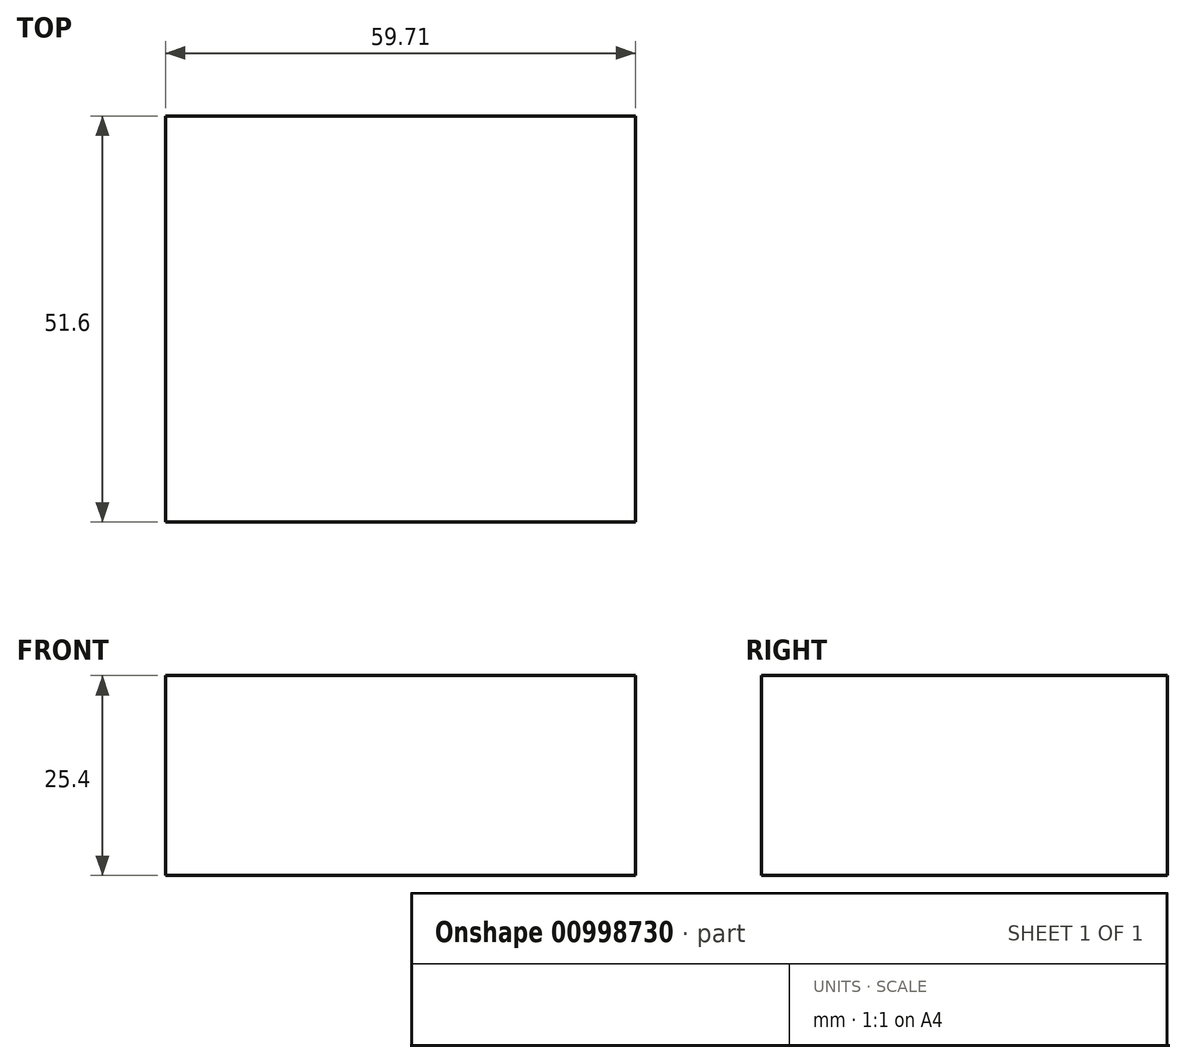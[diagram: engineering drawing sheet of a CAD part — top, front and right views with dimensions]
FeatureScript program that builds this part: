
annotation { "Feature Type Name" : "Feature", "Feature Type Description" : "" }
export const myFeature = defineFeature(function(context is Context, id is Id, definition is map)
    precondition{}
    {
        {
            var Q0;
            Q0=qCreatedBy(makeId("Top.planeOp"),FACE);
            var sketch = newSketch(context, id + "F0", { "sketchPlane" : qUnion([Q0])});
            skLineSegment(sketch, "E0.bottom", {"start": v(-91.76, -40.56) * mm, "end": v(-187.36, -40.56) * mm});
            skLineSegment(sketch, "E0.top", {"start": v(-91.76, 11.04) * mm, "end": v(-187.36, 11.04) * mm});
            skLineSegment(sketch, "E0.left", {"start": v(-91.76, -40.56) * mm, "end": v(-91.76, 11.04) * mm});
            skLineSegment(sketch, "E0.right", {"start": v(-187.36, -40.56) * mm, "end": v(-187.36, 11.04) * mm});
            skPoint(sketch, "E0.middle", {"position": v(-139.56, -14.76) * mm});
            skLineSegment(sketch, "E1.bottom", {"start": v(-121.22, 105.1) * mm, "end": v(-127.65, 105.1) * mm});
            skLineSegment(sketch, "E1.top", {"start": v(-121.22, -156.9) * mm, "end": v(-127.65, -156.9) * mm});
            skLineSegment(sketch, "E1.left", {"start": v(-121.22, 105.1) * mm, "end": v(-121.22, -156.9) * mm});
            skLineSegment(sketch, "E1.right", {"start": v(-127.65, 105.1) * mm, "end": v(-127.65, -156.9) * mm});
            skPoint(sketch, "E1.middle", {"position": v(-124.43, -25.9) * mm});
            skSolve(sketch);
        }
        {
            var Q0;
            {var subQ0=sQuery(id+"F0.wireOp",EDGE,"E0.right");Q0=makeQuery(id+"F0.imprint","IMPRINT",FACE,{"disambiguationData":[TD([[makeQuery(id+"F0.imprint","IMPRINT",EDGE,{"derivedFrom":subQ0}),-1.0]])]});}
            var Q1;
            Q1=sQuery(id+"F0.wireOp",EDGE,"E1.left");
            var Q2;
            Q2=sQuery(id+"F0.wireOp",EDGE,"E1.right");
            extrude(context, id + "F1", {"entities" : qUnion([Q0]), "surfaceEntities" : qUnion([Q1, Q2]), "depth" : 25.4 * mm, "offsetDistance" : 25.4 * mm});
        }
    });
